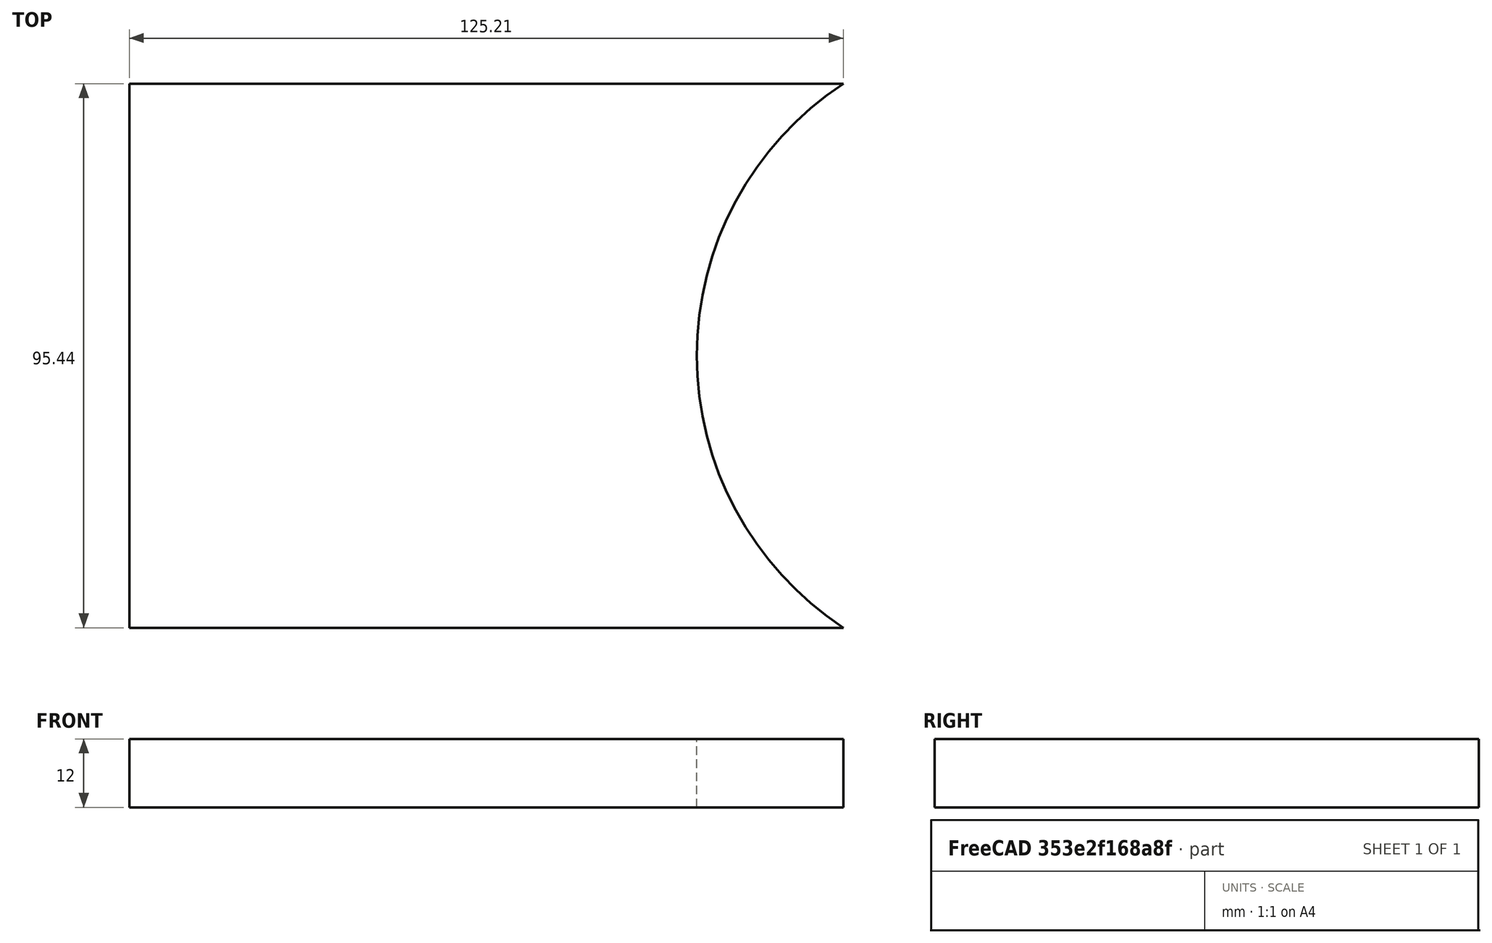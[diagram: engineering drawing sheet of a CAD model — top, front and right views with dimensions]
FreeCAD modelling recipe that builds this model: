
FCSTD DOCUMENT  (FreeCAD 0.21R33675 (Git))
Label: YawBearing_SafetyCatch
License: All rights reserved
LicenseURL: http://en.wikipedia.org/wiki/All_rights_reserved
objects: Sketcher::SketchObject×1, PartDesign::Pad×1, PartDesign::Body×1, Spreadsheet::Sheet×1
note: 4 computed .brp shape members not serialized (recipe doc carries the construction recipe); baked Part::Feature solids carry a one-line shape summary decoded from their .brp
EXTERNAL_REF file=../Master_of_Puppets.FCStd obj=HighEndStop
EXTERNAL_REF file=../Master_of_Puppets.FCStd obj=Spreadsheet

FEATURE [Sketcher::SketchObject] Sketch
  FullyConstrained = true
  MapMode = 5
  Placement = pos=(0,0,0) rot=(0,1,0;3.14159rad)
  Support = -> [XY_Plane]
  expr: Constraints[14] = Spreadsheet.Width
  expr: Constraints[15] = Spreadsheet.Length
  expr: Constraints[1] = Spreadsheet.YawPipeRadius
  sketch-geometry (6):
    g0: LineSegment StartX=156.662 StartY=47.7203 StartZ=0 EndX=156.662 EndY=-47.7203 EndZ=0
    g1: LineSegment StartX=57.15 StartY=-47.7203 StartZ=0 EndX=57.15 EndY=47.7202 EndZ=0
    g2: Circle CenterX=0 CenterY=0 CenterZ=0 NormalX=0 NormalY=0 NormalZ=1 AngleXU=0 Radius=57.15
    g3: LineSegment StartX=156.662 StartY=47.7203 StartZ=0 EndX=31.4468 EndY=47.7203 EndZ=0
    g4: LineSegment StartX=156.662 StartY=-47.7203 StartZ=0 EndX=31.4468 EndY=-47.7203 EndZ=0
    g5: ArcOfCircle CenterX=0 CenterY=0 CenterZ=0 NormalX=0 NormalY=0 NormalZ=1 AngleXU=0 Radius=57.15 StartAngle=5.29505 EndAngle=7.27132
  constraints (17):
    c: Symmetric(g0,g0,g-1)
    c: Radius(g2) = 57.15
    c: Tangent(g2,g1)
    c: PointOnObject(g3,g2)
    c: Horizontal(g3)
    c: Coincident(g5,g2)
    c: Coincident(g5,g3)
    c: Coincident(g5,g4)
    c: Horizontal(g4)
    c: Coincident(g4,g0)
    c: Coincident(g3,g0)
    c: Vertical(g1)
    c: PointOnObject(g1,g3)
    c: PointOnObject(g1,g4)
    c: DistanceY(g0,g0) = 95.4405
    c: DistanceX(g1,g0) = 99.5122
    c: Coincident(g5,g-1)
FEATURE [PartDesign::Pad] Pad
  Direction = (0,0,-1)
  Length = 12
  Length2 = 100
  Profile = -> Sketch
  Type = 0
  expr: Length = Spreadsheet.FlatMetalThickness
FEATURE [PartDesign::Body] Body  label="YawBearing_SafetyCatch"
  Group = -> [Sketch,Pad]
  Openafpm_Flat = true
  Origin = -> Origin
  Tip = -> Pad
FEATURE [Spreadsheet::Sheet] Spreadsheet
  cells = A1='Inputs; A2='FlatMetalThickness; B2(FlatMetalThickness)==Master_of_Puppets#Spreadsheet.FlatMetalThickness; A3='YawPipeDiameter; B3(YawPipeDiameter)==Master_of_Puppets#Spreadsheet.YawPipeDiameter; A4='CalculatedWindTurbineShape; B4(CalculatedWindTurbineShape)==Master_of_Puppets#Spreadsheet.CalculatedWindTurbineShape; A5='Width; B5(Width)==Master_of_Puppets#HighEndStop.SafetyCatchWidth; A6='Length; B6(Length)==Master_of_Puppets#HighEndStop.SafetyCatchLength; A7='Calculated; A8='YawPipeRadius; B8(YawPipeRadius)==YawPipeDiameter / 2; A9='DistanceFromOrigin; B9(DistanceFromOrigin)==CalculatedWindTurbineShape == <<T>> ? 0 : YawPipeRadius
